# Revit family: Drain_Floor_Adjustable_Top-Zurn-Z521-Heavy-Duty
name_source: partatom
category: Plumbing Fixtures
units: mm (PartAtom-declared; Revit-internal decimal feet)

## family parameters
Always vertical = Yes
Cut with Voids When Loaded = No
Maintain Annotation Orientation = No
OmniClass Number = 23.45.55.21
OmniClass Title = Drains (Wastes)
Part Type = Normal
Room Calculation Point = No
Round Connector Dimension = Use Radius
Shared = No
Work Plane-Based = No

## types (22) — shared parameters
Assembly Code = D2030300
CW Connection = No
Default Elevation = 20 "
Description = 12-1/4 [311] DIAMETER TOP ADJUSTABLE HEAVY-DUTY DRAIN
Grate Open Area = 33 '
HW Connection = No
Main Material = Iron - Zurn - Cast - Painted - Blue
Manufacturer = Zurn Water, LLC
Manufacurer Brand = Zurn
Modified Date = 02/27/2026
Product Documentation Link = https://files.zurn.com
Product Page URL = https://www.zurn.com
Product data url = https://www.bimobject.com
URL = www.zurn.com
Vent Connection = No
WFU = 1
Waste Connection = Yes
zero-valued in all types: CWFU, HWFU

## per-type parameters (varying)
| type | Approx. Weight (Lbs) | Body Height_E | Connector Radius | Model | Pipe Size_A Inside Diameter | Pipe Size_A Nominal Diameter | Pipe Size_A Outer Diameter | Top Material | Type Comments | Width | Z | ZN |
| Z521 3IC | 60 " | 5.25 " | 1.5 " | Z521 | 3.068 " | 3 " | 3.5 " | Iron - Zurn - Cast - Painted - Blue | Z521 3 Inch Inside Caulk | 12.25 " | Yes | No |
| Z521 4IC | 60 " | 5.25 " | 2 " | Z521 | 4.026 " | 4 " | 4.5 " | Iron - Zurn - Cast - Painted - Blue | Z521 4 Inch Inside Caulk | 12.25 " | Yes | No |
| Z521 6IC | 57 " | 5.25 " | 3 " | Z521 | 6.065 " | 6 " | 6.625 " | Iron - Zurn - Cast - Painted - Blue | Z521 6 Inch Inside Caulk | 12.25 " | Yes | No |
| Z521 2NH | 60 " | 5.25 " | 1 " | Z521 | 2.067 " | 2 " | 2.375 " | Iron - Zurn - Cast - Painted - Blue | Z521 2 Inch No-Hub | 12.25 " | Yes | No |
| Z521 3NH | 60 " | 5.25 " | 1.5 " | Z521 | 3.068 " | 3 " | 3.5 " | Iron - Zurn - Cast - Painted - Blue | Z521 3 Inch No-Hub | 12.25 " | Yes | No |
| Z521 4NH | 60 " | 5.25 " | 2 " | Z521 | 4.026 " | 4 " | 4.5 " | Iron - Zurn - Cast - Painted - Blue | Z521 4 Inch No-Hub | 12.25 " | Yes | No |
| Z521 6NH | 57 " | 5.25 " | 3 " | Z521 | 6.065 " | 6 " | 6.625 " | Iron - Zurn - Cast - Painted - Blue | Z521 6 Inch No-Hub | 12.25 " | Yes | No |
| Z521 8NH | 58 " | 5.25 " | 4 " | Z521 | 7.981 " | 8 " | 8.625 " | Iron - Zurn - Cast - Painted - Blue | Z521 8 Inch No-Hub | 12.25 " | Yes | No |
| Z521 2NL | 60 " | 4.625 " | 1 " | Z521 | 2.067 " | 2 " | 2.375 " | Iron - Zurn - Cast - Painted - Blue | Z521 2 Inch Neo-Loc | 12.25 " | Yes | No |
| Z521 3NL | 60 " | 4.625 " | 1.5 " | Z521 | 3.068 " | 3 " | 3.5 " | Iron - Zurn - Cast - Painted - Blue | Z521 3 Inch Neo-Loc | 12.25 " | Yes | No |
| Z521 4NL | 60 " | 4.625 " | 2 " | Z521 | 4.026 " | 4 " | 4.5 " | Iron - Zurn - Cast - Painted - Blue | Z521 4 Inch Neo-Loc | 12.25 " | Yes | No |
| ZN521 3IC | 60 " | 5.25 " | 1.5 " | ZN521 | 3.068 " | 3 " | 3.5 " | Bronze - Zurn - Polished Nickel | ZN521 3 Inch Inside Caulk | 12.93 " | No | Yes |
| ZN521 4IC | 60 " | 5.25 " | 2 " | ZN521 | 4.026 " | 4 " | 4.5 " | Bronze - Zurn - Polished Nickel | ZN521 4 Inch Inside Caulk | 12.93 " | No | Yes |
| ZN521 6IC | 57 " | 5.25 " | 3 " | ZN521 | 6.065 " | 6 " | 6.625 " | Bronze - Zurn - Polished Nickel | ZN521 6 Inch Inside Caulk | 12.93 " | No | Yes |
| ZN521 2NH | 60 " | 5.25 " | 1 " | ZN521 | 2.067 " | 2 " | 2.375 " | Bronze - Zurn - Polished Nickel | ZN521 2 Inch No-Hub | 12.93 " | No | Yes |
| ZN521 3NH | 60 " | 5.25 " | 1.5 " | ZN521 | 3.068 " | 3 " | 3.5 " | Bronze - Zurn - Polished Nickel | ZN521 3 Inch No-Hub | 12.93 " | No | Yes |
| ZN521 4NH | 60 " | 5.25 " | 2 " | ZN521 | 4.026 " | 4 " | 4.5 " | Bronze - Zurn - Polished Nickel | ZN521 4 Inch No-Hub | 12.93 " | No | Yes |
| ZN521 6NH | 57 " | 5.25 " | 3 " | ZN521 | 6.065 " | 6 " | 6.625 " | Bronze - Zurn - Polished Nickel | ZN521 6 Inch No-Hub | 12.93 " | No | Yes |
| ZN521 8NH | 58 " | 5.25 " | 4 " | ZN521 | 7.981 " | 8 " | 8.625 " | Bronze - Zurn - Polished Nickel | ZN521 8 Inch No-Hub | 12.93 " | No | Yes |
| ZN521 2NL | 60 " | 4.625 " | 1 " | ZN521 | 2.067 " | 2 " | 2.375 " | Bronze - Zurn - Polished Nickel | ZN521 2 Inch Neo-Loc | 12.93 " | No | Yes |
| ZN521 3NL | 60 " | 4.625 " | 1.5 " | ZN521 | 3.068 " | 3 " | 3.5 " | Bronze - Zurn - Polished Nickel | ZN521 3 Inch Neo-Loc | 12.93 " | No | Yes |
| ZN521 4NL | 60 " | 4.625 " | 2 " | ZN521 | 4.026 " | 4 " | 4.5 " | Bronze - Zurn - Polished Nickel | ZN521 4 Inch Neo-Loc | 12.93 " | No | Yes |

## geometry (parser evidence)
native form markers: Blend x4, Sweep x4
no freeform markers — native parametric forms only
